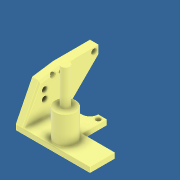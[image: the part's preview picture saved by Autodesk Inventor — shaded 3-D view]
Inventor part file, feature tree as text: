
AUTODESK INVENTOR PART (.ipt)
format: ipt  version: 2020 (Build 240168000, 168)  size: 315,904 bytes
history: native  units: mm
features: sketch x13, extrude x12, chamfer x3, projected_geometry x3, plane x1, pattern_circular x1, loft x1, fillet x1, other x1
ambient origin geometry x8: Origin, YZ Plane, XZ Plane, XY Plane, X Axis, Y Axis, Z Axis, Center Point
bodies: Solid1 (feature_tree)
feature tree (36):
  plane  "Work Plane1"
  extrude  "Extrusion1"  Depth=32.0mm TaperAngle=0.0deg
  extrude  "Extrusion3"  Depth=27.0mm TaperAngle=0.0deg
  extrude  "Extrusion9"  Depth=24.0mm
  pattern_circular  "Circular Pattern1"  Count=4 Angle=360.0deg
  extrude  "Extrusion11"  Depth=8.0mm
  extrude  "Extrusion12"  Depth=8.0mm
  chamfer  "Chamfer4"  Distance=48.0mm
  chamfer  "Chamfer5"  Distance=32.0mm Angle=45.0deg
  chamfer  "Chamfer6"  Distance=20.0mm Angle=45.0deg
  extrude  "Extrusion13"  Depth=6.0mm TaperAngle=0.0deg
  loft  "Loft1"
  extrude  "Extrusion14"  Depth=4.8mm
  fillet  "Fillet1"  Radius=4.8mm
  extrude  "Extrusion15"  Depth=4.8mm
  extrude  "Extrusion16"  Depth=8.0mm
  extrude  "Extrusion17"  Depth=8.0mm
  extrude  "Extrusion19"  Depth=32.0mm
  extrude  "Extrusion20"  Depth=5.0mm
  sketch  "Sketch1"  dims[d0=8.0mm d2=32.0mm d3=0.0mm]
  sketch  "Sketch5"  dims[d17=20.0mm d18=27.0mm d19=0.0mm]
  sketch  "Sketch17"  dims[d86=72.0mm d87=24.0mm]
  sketch  "Sketch19"  dims[d88=5.0mm d89=0.0mm d93=40.0mm d94=360.0deg]
  sketch  "Sketch20"  dims[d103=8.0mm d104=8.0mm]
  sketch  "Sketch21"  dims[d105=35.0mm d106=0.0mm d107=8.0mm]
  sketch  "Sketch23"  dims[d108=40.0mm d109=48.0mm d110=0.0mm d111=32.0mm d112=20.0mm d113=45.0deg d114=20.0mm d115=3.0mm d116=45.0deg]
  other  "Edges1"
  sketch  "Sketch24"  dims[d117=2.0mm d118=3.0mm d119=45.0deg d120=6.0mm d121=0.0mm]
  sketch  "Sketch25"  dims[d122=0.0mm d123=90.0deg d124=0.0mm d125=90.0deg]
  sketch  "Sketch27"  dims[d126=4.8mm d127=4.8mm d128=4.8mm]
  projected_geometry  "Projected Loop1"
  sketch  "Sketch28"  dims[d129=4.8mm d130=4.8mm]
  projected_geometry  "Projected Loop2"
  sketch  "Sketch31"  dims[d131=8.0mm d132=8.0mm]
  projected_geometry  "Projected Loop4"
  sketch  "Sketch33"  dims[d133=8.0mm d134=8.0mm d135=32.0mm d136=20.0mm d137=16.0mm d138=0.0mm d139=0.7mm d140=4.8mm d141=32.0mm d142=16.0mm d143=0.0mm d144=32.0mm d145=0.0mm d146=8.0mm d147=0.0mm d154=8.0mm d155=0.0mm d156=16.0mm d157=5.0mm d158=0.0mm d161=0.5mm d162=0.872665mm d163=0.5mm d164=0.872665mm]
